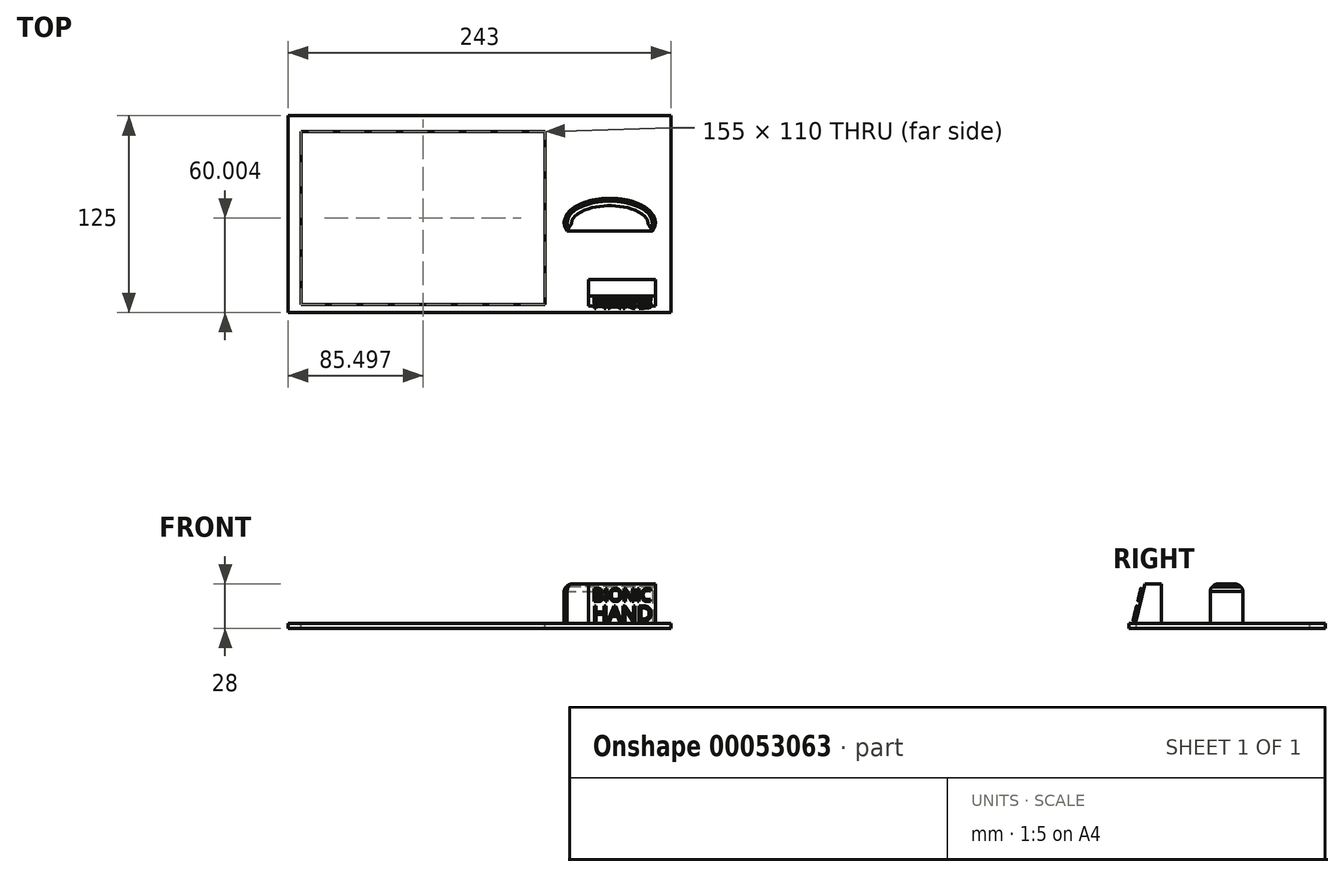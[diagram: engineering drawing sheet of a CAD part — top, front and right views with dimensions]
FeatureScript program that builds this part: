
annotation { "Feature Type Name" : "Feature", "Feature Type Description" : "" }
export const myFeature = defineFeature(function(context is Context, id is Id, definition is map)
    precondition{}
    {
        {
            var Q0;
            Q0=qCreatedBy(makeId("Top.planeOp"),FACE);
            var sketch = newSketch(context, id + "F16", { "sketchPlane" : qUnion([Q0])});
            skLineSegment(sketch, "E0.bottom", {"start": v(-89.64, -79.38) * mm, "end": v(60.36, -79.38) * mm});
            skLineSegment(sketch, "E0.top", {"start": v(-89.64, 20.62) * mm, "end": v(60.36, 20.62) * mm});
            skLineSegment(sketch, "E0.left", {"start": v(-89.64, -79.38) * mm, "end": v(-89.64, 20.62) * mm});
            skLineSegment(sketch, "E0.right", {"start": v(60.36, -79.38) * mm, "end": v(60.36, 20.62) * mm});
            skSolve(sketch);
        }
        {
            var Q0;
            Q0=makeQuery(id+"F16.imprint","IMPRINT",FACE,{"disambiguationData":[TD([[makeQuery(id+"F16.imprint","IMPRINT",EDGE,{"derivedFrom":sQuery(id+"F16.wireOp",EDGE,"E0.bottom")}),1.0]])]});
            extrude(context, id + "F0", {"entities" : qUnion([Q0]), "depth" : 3 * mm});
        }
        {
            var Q0;
            Q0=makeQuery(id+"F0.opExtrude","CAP_FACE",FACE,{"disambiguationData":[OSD([sQuery(id+"F16.wireOp",EDGE,"E0.bottom"),sQuery(id+"F16.wireOp",EDGE,"E0.top"),sQuery(id+"F16.wireOp",EDGE,"E0.left"),sQuery(id+"F16.wireOp",EDGE,"E0.right")])],"isStart":false});
            var sketch = newSketch(context, id + "F1", { "sketchPlane" : qUnion([Q0])});
            skLineSegment(sketch, "E1.bottom", {"start": v(8.07, -79.38) * mm, "end": v(50.66, -79.38) * mm});
            skLineSegment(sketch, "E1.top", {"start": v(8.07, -58.55) * mm, "end": v(50.66, -58.55) * mm});
            skLineSegment(sketch, "E1.left", {"start": v(8.07, -79.38) * mm, "end": v(8.07, -58.55) * mm});
            skLineSegment(sketch, "E1.right", {"start": v(50.66, -79.38) * mm, "end": v(50.66, -58.55) * mm});
            skSolve(sketch);
        }
        {
            var Q0;
            Q0=makeQuery(id+"F1.imprint","IMPRINT",FACE,{"disambiguationData":[TD([[makeQuery(id+"F1.imprint","IMPRINT",EDGE,{"derivedFrom":sQuery(id+"F1.wireOp",EDGE,"E1.bottom")}),1.0]])]});
            extrude(context, id + "F2", {"entities" : qUnion([Q0]), "operationType" : NewBodyOperationType.ADD, "depth" : 25 * mm});
        }
        {
            var Q0;
            Q0=makeQuery(id+"F2.opExtrude","SWEPT_FACE",FACE,{"disambiguationData":[OSD([sQuery(id+"F1.wireOp",EDGE,"E1.right")])]});
            var sketch = newSketch(context, id + "F3", { "sketchPlane" : qUnion([Q0])});
            skLineSegment(sketch, "E2", {"start": v(-79.38, 3) * mm, "end": v(-79.38, 28) * mm});
            skLineSegment(sketch, "E3", {"start": v(-75.1, 3) * mm, "end": v(-68.96, 28) * mm});
            skSolve(sketch);
        }
        {
            var Q0;
            {var subQ0=sQuery(id+"F3.wireOp",EDGE,"E2");Q0=makeQuery(id+"F3.imprint","IMPRINT",FACE,{"disambiguationData":[TD([[makeQuery(id+"F3.imprint","IMPRINT",EDGE,{"derivedFrom":subQ0}),1.0]])]});}
            extrude(context, id + "F17", {"entities" : qUnion([Q0]), "operationType" : NewBodyOperationType.REMOVE, "oppositeDirection" : true, "depth" : 78.8 * mm});
        }
        {
            var Q0;
            Q0=makeQuery(id+"F17.boolean.opBoolean","COPY",FACE,{"derivedFrom":makeQuery(id+"F17.opExtrude","SWEPT_FACE",FACE,{"disambiguationData":[OSD([sQuery(id+"F3.wireOp",EDGE,"E3")])]})});
            var sketch = newSketch(context, id + "F4", { "sketchPlane" : qUnion([Q0])});
            skText(sketch, "E4", { "text": "BIONIC", "fontName": "OpenSans-Regular.ttf"});
            skText(sketch, "E5", { "text": "HAND", "fontName": "OpenSans-Regular.ttf"});
            const initialGuessF4  = {"E4": [0.01053, -0.0006, 1, 0, 0.00803], "E5": [0.01053, -0.01349, 1, 0, 0.0096]};
            skSetInitialGuess(sketch, initialGuessF4);
            skSolve(sketch);
        }
        {
            var Q0;
            Q0 = qSketchRegion(id + "F4", true);
            extrude(context, id + "F5", {"entities" : qUnion([Q0]), "operationType" : NewBodyOperationType.ADD, "depth" : 2 * mm});
        }
        {
            var Q0;
            {var subQ0=sQuery(id+"F1.wireOp",EDGE,"E1.right");var subQ1=makeQuery(id+"F2.opExtrude","CAP_EDGE",EDGE,{"disambiguationData":[OSD([subQ0])],"isStart":true});Q0=makeQuery(id+"F17.boolean.opBoolean","MERGE",FACE,{"derivedFrom":[makeQuery(id+"F0.opExtrude","CAP_FACE",FACE,{"disambiguationData":[OSD([sQuery(id+"F16.wireOp",EDGE,"E0.bottom"),sQuery(id+"F16.wireOp",EDGE,"E0.top"),sQuery(id+"F16.wireOp",EDGE,"E0.left"),sQuery(id+"F16.wireOp",EDGE,"E0.right")])],"isStart":false}),makeQuery(id+"F17.opExtrude","SWEPT_FACE",FACE,{"disambiguationData":[OSD([subQ0]),TDD([makeQuery(id+"F3.imprint","IMPRINT",EDGE,{"disambiguationData":[TD([[makeQuery(id+"F3.imprint","INTERSECT",VERTEX,{"derivedFrom":[subQ1,sQuery(id+"F3.wireOp",EDGE,"E2")]}),-1.0]])],"derivedFrom":subQ1})])]})]});}
            var sketch = newSketch(context, id + "F6", { "sketchPlane" : qUnion([Q0])});
            skEllipticalArc(sketch, "E6", {});
            skLineSegment(sketch, "E7", {"start": v(-5.47, -27.64) * mm, "end": v(48.57, -27.64) * mm});
            const initialGuessF6  = {"E6": [0.021547388285398483, -0.02214759960770607, 1, 0, 0.028957732021808624, 0.015280321405560042, 5.915336773261316, 3.5094411875080636]};
            skSetInitialGuess(sketch, initialGuessF6);
            skSolve(sketch);
        }
        {
            var Q0;
            Q0=makeQuery(id+"F6.imprint","IMPRINT",FACE,{"disambiguationData":[TD([[makeQuery(id+"F6.imprint","IMPRINT",EDGE,{"derivedFrom":sQuery(id+"F6.wireOp",EDGE,"E6")}),1.0]])]});
            extrude(context, id + "F7", {"entities" : qUnion([Q0]), "operationType" : NewBodyOperationType.ADD, "depth" : 25 * mm});
        }
        {
            var Q0;
            Q0=makeQuery(id+"F7.opExtrude","CAP_FACE",FACE,{"disambiguationData":[OSD([sQuery(id+"F6.wireOp",EDGE,"E6"),sQuery(id+"F6.wireOp",EDGE,"E7")])],"isStart":false});
            chamfer(context, id + "F8", {"entities" : qUnion([Q0]), "width" : 3 * mm, "tangentPropagation" : true});
        }
        {
            var Q0;
            Q0=makeQuery(id+"F7.opExtrude","CAP_FACE",FACE,{"disambiguationData":[OSD([sQuery(id+"F6.wireOp",EDGE,"E6"),sQuery(id+"F6.wireOp",EDGE,"E7")])],"isStart":false});
            var Q1;
            {var subQ0=sQuery(id+"F6.wireOp",EDGE,"E7");Q1=makeQuery(id+"F8.opChamfer","BLEND_EDGE",EDGE,{"blendedFrom":[makeQuery(id+"F7.opExtrude","CAP_EDGE",EDGE,{"disambiguationData":[OSD([subQ0])],"isStart":false}),makeQuery(id+"F7.opExtrude","SWEPT_FACE",FACE,{"disambiguationData":[OSD([subQ0])]})],"blendedInto":[makeQuery(id+"F7.opExtrude","SWEPT_FACE",FACE,{"disambiguationData":[OSD([subQ0])]})]});}
            var Q2;
            {var subQ0=sQuery(id+"F6.wireOp",EDGE,"E6");Q2=makeQuery(id+"F8.opChamfer","BLEND_EDGE",EDGE,{"blendedFrom":[makeQuery(id+"F7.opExtrude","CAP_EDGE",EDGE,{"disambiguationData":[OSD([subQ0])],"isStart":false}),makeQuery(id+"F7.opExtrude","SWEPT_FACE",FACE,{"disambiguationData":[OSD([subQ0])]})],"blendedInto":[makeQuery(id+"F7.opExtrude","SWEPT_FACE",FACE,{"disambiguationData":[OSD([subQ0])]})]});}
            fillet(context, id + "F9", {"entities" : qUnion([Q0, Q1, Q2]), "radius" : 4 * mm, "tangentPropagation" : true, "allowEdgeOverflow" : false});
        }
        {
            var Q0;
            Q0=makeQuery(id+"F0.opExtrude","SWEPT_FACE",FACE,{"disambiguationData":[OSD([sQuery(id+"F16.wireOp",EDGE,"E0.left")])]});
            extrude(context, id + "F10", {"entities" : qUnion([Q0]), "operationType" : NewBodyOperationType.ADD, "depth" : 50 * mm});
        }
        {
            var Q0;
            {var subQ0=sQuery(id+"F16.wireOp",EDGE,"E0.left");var subQ1=sQuery(id+"F1.wireOp",EDGE,"E1.right");var subQ2=makeQuery(id+"F2.opExtrude","CAP_EDGE",EDGE,{"disambiguationData":[OSD([subQ1])],"isStart":true});Q0=makeQuery(id+"F10.boolean.opBoolean","MERGE",FACE,{"derivedFrom":[makeQuery(id+"F17.boolean.opBoolean","MERGE",FACE,{"derivedFrom":[makeQuery(id+"F0.opExtrude","CAP_FACE",FACE,{"disambiguationData":[OSD([sQuery(id+"F16.wireOp",EDGE,"E0.bottom"),sQuery(id+"F16.wireOp",EDGE,"E0.top"),subQ0,sQuery(id+"F16.wireOp",EDGE,"E0.right")])],"isStart":false}),makeQuery(id+"F17.opExtrude","SWEPT_FACE",FACE,{"disambiguationData":[OSD([subQ1]),TDD([makeQuery(id+"F3.imprint","IMPRINT",EDGE,{"disambiguationData":[TD([[makeQuery(id+"F3.imprint","INTERSECT",VERTEX,{"derivedFrom":[subQ2,sQuery(id+"F3.wireOp",EDGE,"E2")]}),-1.0]])],"derivedFrom":subQ2})])]})]}),makeQuery(id+"F10.opExtrude","SWEPT_FACE",FACE,{"disambiguationData":[OSD([subQ0]),TDD([makeQuery(id+"F0.opExtrude","CAP_EDGE",EDGE,{"disambiguationData":[OSD([subQ0])],"isStart":false})])]})]});}
            var sketch = newSketch(context, id + "F11", { "sketchPlane" : qUnion([Q0])});
            skLineSegment(sketch, "E8.bottom", {"start": v(-174.64, -74.38) * mm, "end": v(-19.64, -74.38) * mm});
            skLineSegment(sketch, "E8.top", {"start": v(-174.64, 35.62) * mm, "end": v(-19.64, 35.62) * mm});
            skLineSegment(sketch, "E8.left", {"start": v(-174.64, -74.38) * mm, "end": v(-174.64, 35.62) * mm});
            skLineSegment(sketch, "E8.right", {"start": v(-19.64, -74.38) * mm, "end": v(-19.64, 35.62) * mm});
            skSolve(sketch);
        }
        {
            var Q0;
            Q0=makeQuery(id+"F10.opExtrude","CAP_FACE",FACE,{"disambiguationData":[OSD([sQuery(id+"F16.wireOp",EDGE,"E0.left")])],"isStart":false});
            extrude(context, id + "F12", {"entities" : qUnion([Q0]), "operationType" : NewBodyOperationType.ADD, "depth" : 43 * mm});
        }
        {
            var Q0;
            {var subQ0=sQuery(id+"F16.wireOp",EDGE,"E0.left");var subQ1=sQuery(id+"F16.wireOp",EDGE,"E0.top");Q0=makeQuery(id+"F12.boolean.opBoolean","MERGE",FACE,{"derivedFrom":[makeQuery(id+"F10.boolean.opBoolean","MERGE",FACE,{"derivedFrom":[makeQuery(id+"F0.opExtrude","SWEPT_FACE",FACE,{"disambiguationData":[OSD([subQ1])]}),makeQuery(id+"F10.opExtrude","SWEPT_FACE",FACE,{"disambiguationData":[OSD([subQ1,subQ0])]})]}),makeQuery(id+"F12.opExtrude","SWEPT_FACE",FACE,{"disambiguationData":[OSD([subQ1,subQ0])]})]});}
            extrude(context, id + "F13", {"entities" : qUnion([Q0]), "operationType" : NewBodyOperationType.ADD, "depth" : 25 * mm});
        }
        {
            var Q0;
            {var subQ1=sQuery(id+"F11.wireOp",EDGE,"E8.top");Q0=makeQuery(id+"F11.imprint","IMPRINT",FACE,{"disambiguationData":[TD([[makeQuery(id+"F11.imprint","IMPRINT",EDGE,{"derivedFrom":subQ1}),-1.0]])]});}
            var Q1;
            {var subQ0=sQuery(id+"F11.wireOp",EDGE,"E8.right");var subQ1=sQuery(id+"F11.wireOp",EDGE,"E8.bottom");var subQ2=makeQuery(id+"F11.imprint","INTERSECT",VERTEX,{"derivedFrom":[subQ1,subQ0]});Q1=makeQuery(id+"F11.imprint","IMPRINT",FACE,{"disambiguationData":[TD([[makeQuery(id+"F11.imprint","IMPRINT",EDGE,{"disambiguationData":[TD([[subQ2,1.0]])],"derivedFrom":subQ1}),1.0]])]});}
            extrude(context, id + "F14", {"entities" : qUnion([Q0, Q1]), "operationType" : NewBodyOperationType.REMOVE, "oppositeDirection" : true, "depth" : 25 * mm});
        }
    });
